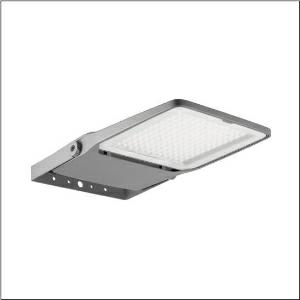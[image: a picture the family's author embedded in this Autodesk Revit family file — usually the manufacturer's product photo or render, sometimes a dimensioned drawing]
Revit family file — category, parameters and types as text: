
# Revit family: floodlight_fl_20_midi___pl52_5xa7682e3d2ac_2b6a
name_source: partatom
category: Lighting Fixtures
units: mm (PartAtom-declared; Revit-internal decimal feet)

## family parameters
Cut with Voids When Loaded = No
Host = Face
Light Source = No
Part Type = Normal
Room Calculation Point = No
Round Connector Dimension = Use Diameter
Shared = No

## types (1)
- --- (1 x LED 5000K / CRI = 70 (unbekannt), 27250 lm, 5000K)
    Apparent Load = 208 VA
    CIE Flux Codes = 27 59 98 100 100
    Color Rendering = 70
    Color Temperature = 5000K
    Default Elevation = 1800 mm
    Description = Floodlight FL 20 midi, floodlight, primary light control with lens, of plastic, primary optical cover: protective disc, of toughened safety glass, transparent, light distribution: PL52, light emission: direct distribution, primary light characteristic: asymmetric, installation type: surface-mounted, LED High Power LED, rated luminous flux: 27.250 lm, light colour: 750, colour temperature: 5000K, control gear: ECG Plus, control: flexible luminous flux parameterisation, time-dependent luminous flux control, digital communication interface, power reduction, overheat protection, electronic power reduction, with terminal, 5-pole, max. 2.5mm², mains connection: 220..240V, AC, 50/60Hz, rated input power: 208W, LED unit, of diecast aluminium, powder-coated, Siteco® metallic grey (DB 702S), length: 731 mm, width: 450 mm, height: 76mm, housing frame, of diecast aluminium, powder-coated, Siteco® metallic grey (DB 702S), wall fastening, of steel, powder-coated, Siteco® metallic grey (DB 702S), DALIprotection rating (complete): IP66, insulation class (complete): insulation class II (safety insulation), certification: CE, ENEC, VDE, protection symbol: D, permissible ambient temperature for indoor applications: -40..+40°C, permissible ambient temperature for outdoor applications: -40..+50°C, standard: DIN EN 12944, packaging unit: 1 piece

Light Distribution: PL52
    Height = 76 mm
    Lamp = 1 x LED 5000K / CRI >= 70 (unbekannt)
    Lamp Light Flux = 27250 lm
    Lamp count = 1
    Length = 731 mm
    Luminous efficacy = 131 lm/W
    Manufacturer = Siteco
    ModVariant = No
    Model = 5XA7682E3D2AC
    Number of Poles = 1
    OnlyDefault = Yes
    Power Factor = 1
    Product Name = Floodlight FL 20 midi | PL52
    Product group = floodlight | pylon top
    ProductGroupID = 6101
    Protection Class = Protection class II
    Protection Degree = IP 66
    RLX_Detail_Level = 1
    RlxData = <blob elided: 92229 chars, md5=77628613>
    Socket = socket
    Standby Power = 0 W
    System Light Flux = 27250 lm
    System Power = 208 W
    Type Comments = factory setting: luminous flux: 100 % | dim-lin: 254 | 484 mA
    Type Image = l_1005944.jpg
    URL = http://relux.com
    VarID = @adj_142825
    Voltage = 0 V
    Weight = 0.00 kg
    Width = 450 mm

## geometry (parser evidence)
native form markers: Blend x4, Sweep x15
no freeform markers — native parametric forms only
